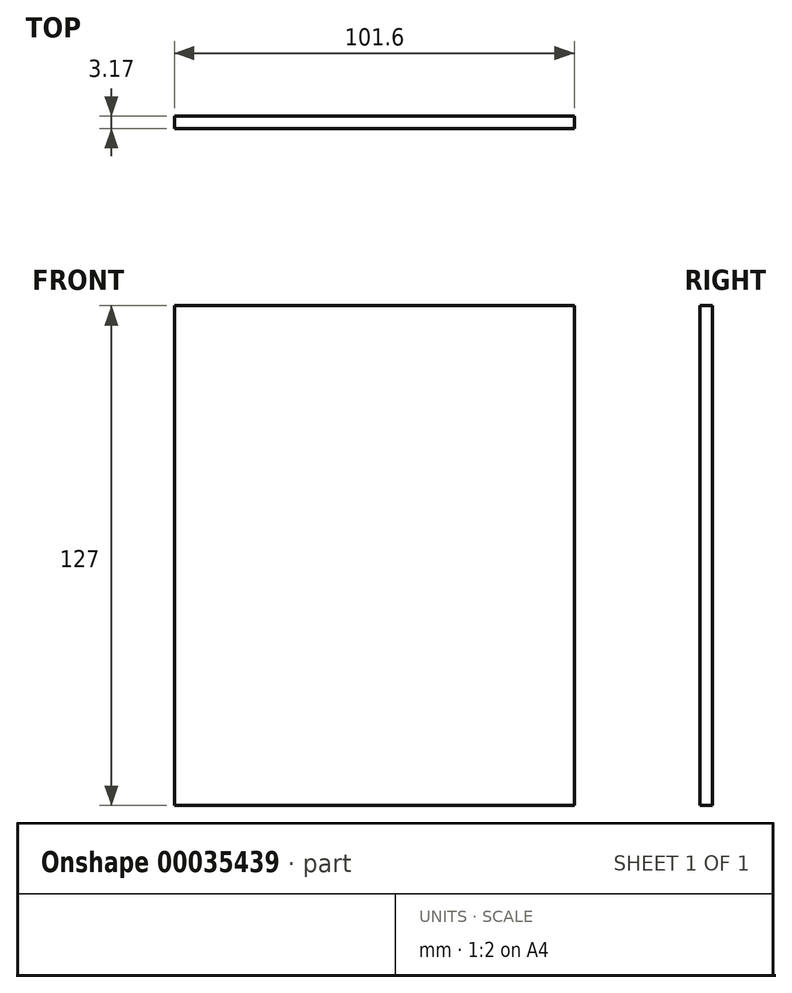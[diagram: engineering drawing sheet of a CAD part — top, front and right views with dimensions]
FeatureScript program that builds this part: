
annotation { "Feature Type Name" : "Feature", "Feature Type Description" : "" }
export const myFeature = defineFeature(function(context is Context, id is Id, definition is map)
    precondition{}
    {
        {
            var Q0;
            Q0=qCreatedBy(makeId("Front.planeOp"),FACE);
            var sketch = newSketch(context, id + "F0", { "sketchPlane" : qUnion([Q0])});
            skLineSegment(sketch, "E0.rect.bottom", {"start": v(50.8, -63.5) * mm, "end": v(-50.8, -63.5) * mm});
            skLineSegment(sketch, "E0.rect.top", {"start": v(50.8, 63.5) * mm, "end": v(-50.8, 63.5) * mm});
            skLineSegment(sketch, "E0.rect.left", {"start": v(50.8, -63.5) * mm, "end": v(50.8, 63.5) * mm});
            skLineSegment(sketch, "E0.rect.right", {"start": v(-50.8, -63.5) * mm, "end": v(-50.8, 63.5) * mm});
            skPoint(sketch, "E0.rect.middle", {"position": v(0, 0) * mm});
            skSolve(sketch);
        }
        {
            var Q0;
            Q0=makeQuery(id+"F0.imprint","IMPRINT",FACE,{"disambiguationData":[TD([[makeQuery(id+"F0.imprint","IMPRINT",EDGE,{"derivedFrom":sQuery(id+"F0.wireOp",EDGE,"E0.rect.bottom")}),-1.0]])]});
            extrude(context, id + "F1", {"entities" : qUnion([Q0]), "depth" : 3.17 * mm});
        }
    });
